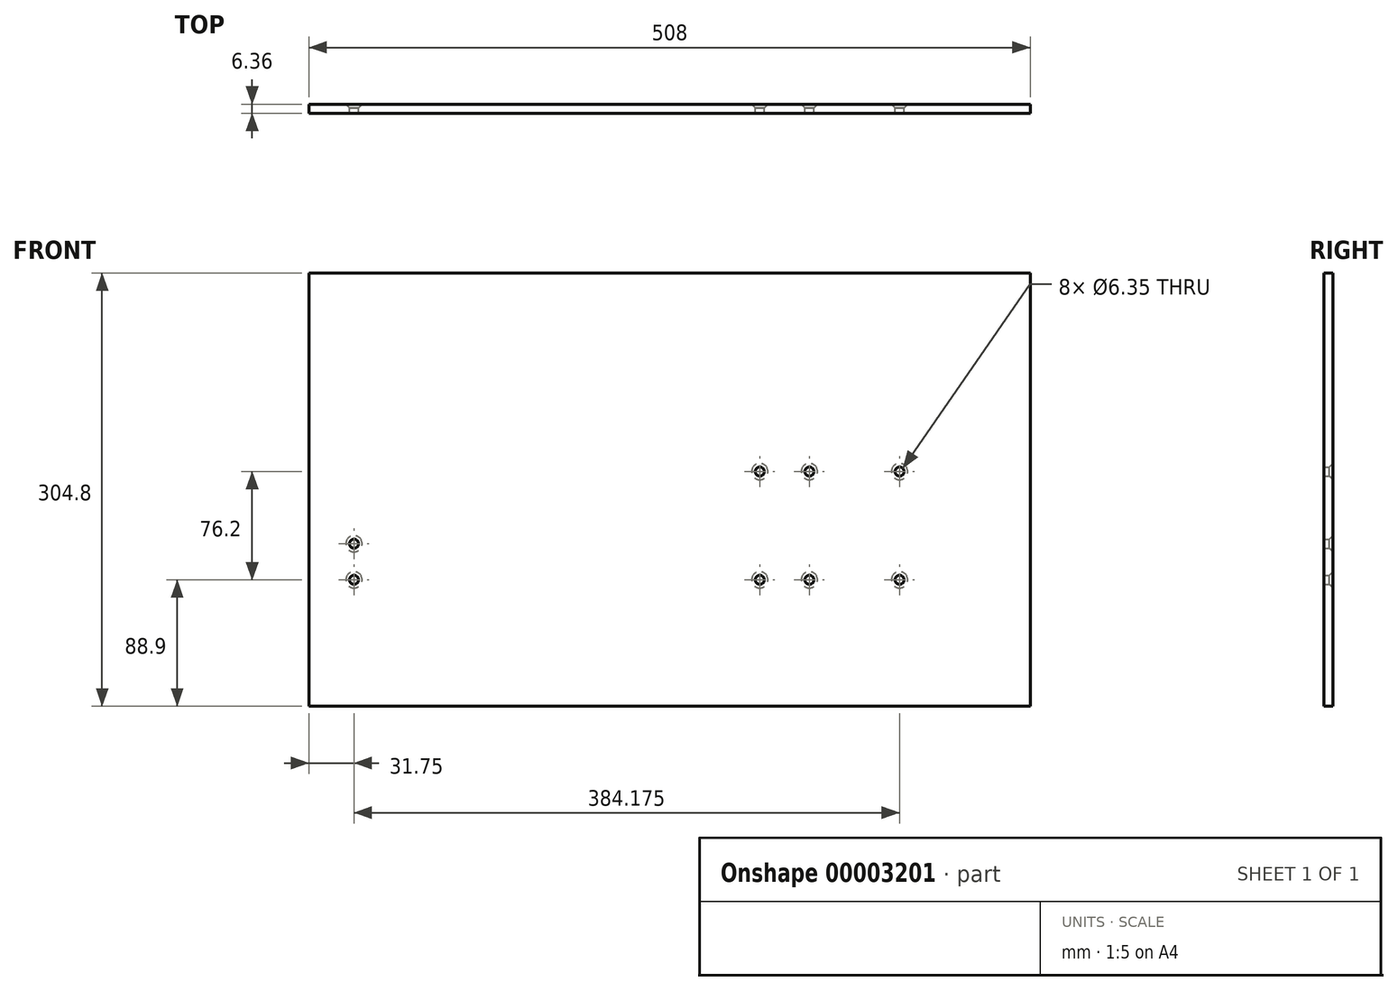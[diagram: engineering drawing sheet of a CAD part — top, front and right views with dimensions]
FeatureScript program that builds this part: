
annotation { "Feature Type Name" : "Feature", "Feature Type Description" : "" }
export const myFeature = defineFeature(function(context is Context, id is Id, definition is map)
    precondition{}
    {
        {
            var Q0;
            Q0=qCreatedBy(makeId("Front.planeOp"),FACE);
            var sketch = newSketch(context, id + "F0", { "sketchPlane" : qUnion([Q0])});
            skLineSegment(sketch, "E0", {"start": v(0, 0) * mm, "end": v(0, -304.8) * mm});
            skLineSegment(sketch, "E1", {"start": v(0, -304.8) * mm, "end": v(508, -304.8) * mm});
            skLineSegment(sketch, "E2", {"start": v(508, -304.8) * mm, "end": v(508, 0) * mm});
            skLineSegment(sketch, "E3", {"start": v(508, 0) * mm, "end": v(0, 0) * mm});
            skLineSegment(sketch, "E4", {"start": v(31.75, 0) * mm, "end": v(31.75, -304.8) * mm, "construction": true});
            skLineSegment(sketch, "E5", {"start": v(317.5, 0) * mm, "end": v(317.5, -304.8) * mm, "construction": true});
            skLineSegment(sketch, "E6", {"start": v(352.43, 0) * mm, "end": v(352.43, -304.8) * mm, "construction": true});
            skLineSegment(sketch, "E7", {"start": v(415.93, 0) * mm, "end": v(415.93, -304.8) * mm, "construction": true});
            skLineSegment(sketch, "E8", {"start": v(0, -215.9) * mm, "end": v(508, -215.9) * mm, "construction": true});
            skLineSegment(sketch, "E9", {"start": v(0, -190.5) * mm, "end": v(508, -190.5) * mm, "construction": true});
            skLineSegment(sketch, "E10", {"start": v(0, -139.7) * mm, "end": v(508, -139.7) * mm, "construction": true});
            skCircle(sketch, "E11", {"center": v(317.5, -215.9) * mm, "radius": 3.18 * mm});
            skCircle(sketch, "E12", {"center": v(317.5, -139.7) * mm, "radius": 3.18 * mm});
            skCircle(sketch, "E13", {"center": v(352.43, -139.7) * mm, "radius": 3.18 * mm});
            skCircle(sketch, "E14", {"center": v(352.43, -215.9) * mm, "radius": 3.18 * mm});
            skCircle(sketch, "E15", {"center": v(415.93, -215.9) * mm, "radius": 3.18 * mm});
            skCircle(sketch, "E16", {"center": v(415.93, -139.7) * mm, "radius": 3.18 * mm});
            skCircle(sketch, "E17", {"center": v(31.75, -215.9) * mm, "radius": 3.18 * mm});
            skCircle(sketch, "E18", {"center": v(31.75, -190.5) * mm, "radius": 3.18 * mm});
            skSolve(sketch);
        }
        {
            var Q0;
            Q0=makeQuery(id+"F0.imprint","IMPRINT",FACE,{"disambiguationData":[TD([[makeQuery(id+"F0.imprint","IMPRINT",EDGE,{"derivedFrom":sQuery(id+"F0.wireOp",EDGE,"E0")}),1.0]])]});
            extrude(context, id + "F1", {"entities" : qUnion([Q0]), "endBound" : BoundingType.SYMMETRIC, "depth" : 6.35 * mm});
        }
        {
            var Q0;
            Q0=makeQuery(id+"F1.opExtrude","CAP_EDGE",EDGE,{"disambiguationData":[OSD([sQuery(id+"F0.wireOp",EDGE,"E16")])],"isStart":true});
            var Q1;
            Q1=makeQuery(id+"F1.opExtrude","CAP_EDGE",EDGE,{"disambiguationData":[OSD([sQuery(id+"F0.wireOp",EDGE,"E13")])],"isStart":true});
            var Q2;
            Q2=makeQuery(id+"F1.opExtrude","CAP_EDGE",EDGE,{"disambiguationData":[OSD([sQuery(id+"F0.wireOp",EDGE,"E12")])],"isStart":true});
            var Q3;
            Q3=makeQuery(id+"F1.opExtrude","CAP_EDGE",EDGE,{"disambiguationData":[OSD([sQuery(id+"F0.wireOp",EDGE,"E11")])],"isStart":true});
            var Q4;
            Q4=makeQuery(id+"F1.opExtrude","CAP_EDGE",EDGE,{"disambiguationData":[OSD([sQuery(id+"F0.wireOp",EDGE,"E14")])],"isStart":true});
            var Q5;
            Q5=makeQuery(id+"F1.opExtrude","CAP_EDGE",EDGE,{"disambiguationData":[OSD([sQuery(id+"F0.wireOp",EDGE,"E15")])],"isStart":true});
            var Q6;
            Q6=makeQuery(id+"F1.opExtrude","CAP_EDGE",EDGE,{"disambiguationData":[OSD([sQuery(id+"F0.wireOp",EDGE,"E17")])],"isStart":true});
            var Q7;
            Q7=makeQuery(id+"F1.opExtrude","CAP_EDGE",EDGE,{"disambiguationData":[OSD([sQuery(id+"F0.wireOp",EDGE,"E18")])],"isStart":true});
            chamfer(context, id + "F2", {"entities" : qUnion([Q0, Q1, Q2, Q3, Q4, Q5, Q6, Q7]), "chamferType" : ChamferType.OFFSET_ANGLE, "width" : 2.54 * mm, "oppositeDirection" : false, "angle" : 45 * degree, "tangentPropagation" : true});
        }
    });
